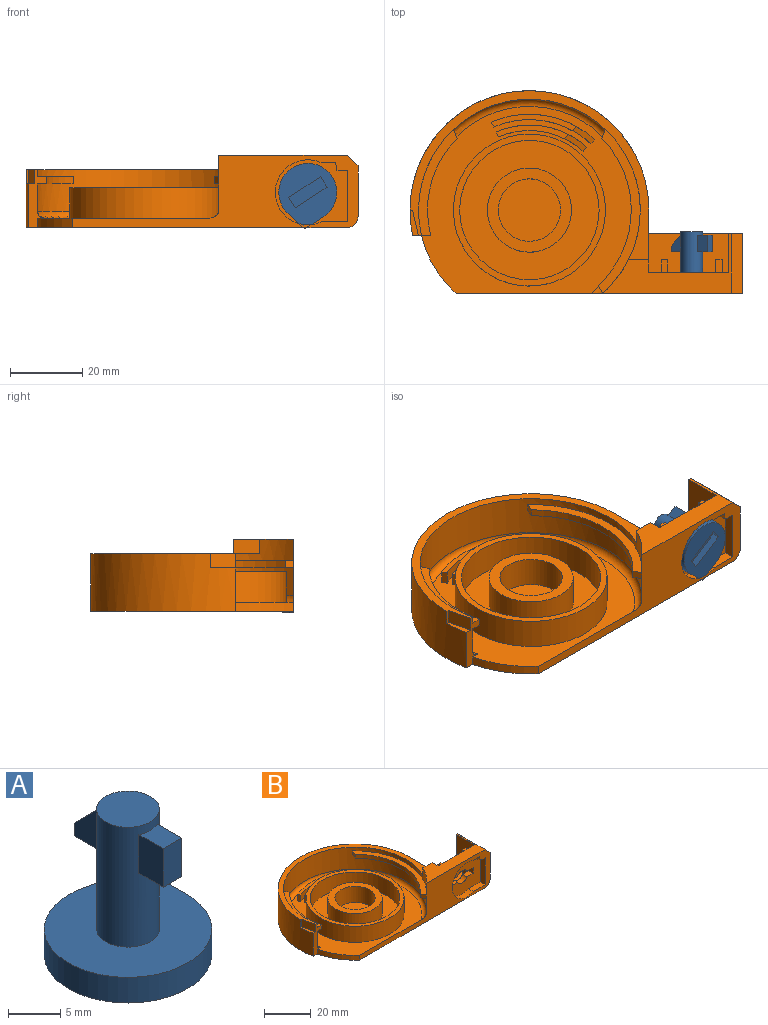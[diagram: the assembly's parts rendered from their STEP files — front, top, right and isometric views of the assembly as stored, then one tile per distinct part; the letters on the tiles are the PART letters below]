
ASSEMBLY  parts=2 mates=1
PART A: 24 faces, bbox 16x16x17 mm
  f0: plane 1.25x0.27mm, normal (0,0,1), area 0.1mm2, adj f11,f19,f23
  f1: plane 6.24x3mm, normal (1,0,0), area 18.7mm2, adj f2,f7,f8,f9
  f2: cylinder r=8mm len=16mm, axis (0,0,1), area 119mm2, adj f1,f7,f8,f9
  f3: plane 10.51x2mm, normal (-1,0,0), area 21mm2, adj f4,f6,f8,f10
  f4: plane 3.4x2mm, normal (0,-1,0), area 6.8mm2, adj f3,f5,f8,f10
  f5: plane 10.51x2mm, normal (1,0,0), area 21mm2, adj f4,f6,f8,f10
  f6: plane 3.4x2mm, normal (0,1,0), area 6.8mm2, adj f3,f5,f8,f10
  f7: plane 6.06x3mm, normal (0.24,0.97,0), area 18.7mm2, adj f1,f2,f8,f9
  f8: plane 16x16mm, normal (0,0,-1), area 172.8mm2, adj f1,f2,f3,f4,f5,f6,f7
  f9: plane 16x16mm, normal (0,0,1), area 180.3mm2, adj f1,f2,f7,f11
  f10: plane 10.51x3.4mm, normal (0,0,-1), area 35.8mm2, adj f3,f4,f5,f6
  f11: cylinder r=3mm len=14mm, axis (0,0,-1), area 240.7mm2, adj f0,f9,f12,f14,f15,f16,f17,f18
  f12: plane 6x6mm, normal (0,0,1), area 28.3mm2, adj f11
  f13: plane 4.5x2.5mm, normal (0,-1,0), area 11.2mm2, adj f14,f15,f16,f17
  f14: plane 4.5x3.27mm, normal (-1,0,0), area 14.7mm2, adj f11,f13,f16,f17
  f15: plane 4.5x3.27mm, normal (1,0,0), area 14.7mm2, adj f11,f13,f16,f17
  f16: plane 3.27x2.5mm, normal (0,0,1), area 7.7mm2, adj f11,f13,f14,f15
  f17: plane 3.27x2.5mm, normal (0,0,-1), area 7.7mm2, adj f11,f13,f14,f15
  f18: plane 4.5x3.27mm, normal (-1,0,0), area 10.2mm2, adj f11,f20,f21,f22,f23
  f19: plane 4.5x3.27mm, normal (1,0,0), area 10.2mm2, adj f0,f11,f20,f21,f23
  f20: plane 2.5x1.5mm, normal (0,1,0), area 3.7mm2, adj f18,f19,f21,f23
  f21: plane 3.27x2.5mm, normal (0,0,-1), area 7.7mm2, adj f11,f18,f19,f20
  f22: plane 1.25x0.27mm, normal (0,0,1), area 0.1mm2, adj f11,f18,f23
  f23: plane 3x3mm, normal (0,0.71,0.71), area 10.6mm2, adj f0,f18,f19,f20,f22
PART B: 75 faces, bbox 92x59.8x20.1 mm
  f0: plane 3.8x2.7mm, normal (0,0,-1), area 10.3mm2, adj f4,f7,f28,f74
  f1: plane 3.8x2.7mm, normal (0,0,-1), area 10.3mm2, adj f5,f7,f28,f74
  f2: plane 3.8x2.7mm, normal (0,0,1), area 10.3mm2, adj f4,f6,f31,f74
  f3: plane 3.8x2.7mm, normal (0,0,1), area 10.3mm2, adj f5,f6,f31,f74
  f4: plane 15.43x6.25mm, normal (1,0,0), area 62.9mm2, adj f0,f2,f11,f28,f31,f36,f37,f74
  f5: plane 15.43x6.25mm, normal (-1,0,0), area 62.9mm2, adj f1,f3,f11,f28,f31,f39,f40,f74
  f6: cylinder r=3.2mm len=5.65mm, axis (0,-1,0), area 18.7mm2, adj f2,f3,f31,f74
  f7: cylinder r=3.2mm len=5.65mm, axis (0,-1,0), area 18.7mm2, adj f0,f1,f28,f74
  f8: cylinder r=30.65mm len=61.3mm, axis (0,0,-1), area 1368.4mm2, adj f9,f10,f19,f25,f26,f56,f57,f59
  f9: plane 16x4.98mm, normal (0,-1,0), area 38.3mm2, adj f8,f10,f20,f21,f24,f27,f41,f43
  f10: plane 66x46.75mm, normal (0,0,1), area 289.6mm2, adj f8,f9,f12,f25,f27,f41,f42
  f11: plane 22x10.8mm, normal (0,0,1), area 225.2mm2, adj f4,f5,f12,f28,f30,f31,f34,f35
  f12: plane 20x17.3mm, normal (1,0,0), area 269.7mm2, adj f10,f11,f24,f25,f26,f27,f28,f34
  f13: plane 38.5x38.5mm, normal (0,0,1), area 739.6mm2, adj f14,f18
  f14: cylinder r=11.62mm len=23.25mm, axis (0,0,-1), area 620.9mm2, adj f13,f17
  f15: plane 17.25x17.25mm, normal (0,0,1), area 233.7mm2, adj f16
  f16: cylinder r=8.62mm len=17.25mm, axis (0,0,-1), area 460.6mm2, adj f15,f17
  f17: plane 23.25x23.25mm, normal (0,0,1), area 190.9mm2, adj f14,f16
  f18: cylinder r=19.25mm len=38.5mm, axis (0,0,-1), area 1028.1mm2, adj f13,f23
  f19: plane 79.01x20.03mm, normal (0,-1,0), area 562mm2, adj f8,f20,f21,f24,f26,f29,f32,f33
  f20: cylinder r=30.65mm len=16mm, axis (0,0,-1), area 47.4mm2, adj f9,f19,f21,f24
  f21: plane 58.49x51.65mm, normal (0,0,1), area 1016.8mm2, adj f9,f19,f20,f22,f45,f46,f47,f48
  f22: cylinder r=21mm len=42mm, axis (0,0,-1), area 1121.5mm2, adj f21,f23
  f23: plane 42x42mm, normal (0,0,1), area 221.3mm2, adj f18,f22
  f24: plane 66x56mm, normal (0,0,-1), area 3117.8mm2, adj f9,f12,f19,f20,f27,f29
  f25: plane 5.61x4mm, normal (0,1,0), area 22.4mm2, adj f8,f10,f12,f26
  f26: plane 35.49x16.5mm, normal (0,0,1), area 218.3mm2, adj f8,f12,f19,f25,f28,f30,f34,f63
  f27: cylinder r=33mm len=66mm, axis (0,0,-1), area 1743.4mm2, adj f9,f10,f12,f24,f42,f43
  f28: plane 22x18.03mm, normal (0,1,0), area 213.7mm2, adj f0,f1,f4,f5,f7,f11,f12,f26
  f29: plane 16.5x0.03mm, normal (-1,0,0), area 0.4mm2, adj f19,f24,f33,f34
  f30: plane 18.03x10.8mm, normal (-1,0,0), area 194.7mm2, adj f11,f26,f28,f34
  f31: plane 13.25x6.21mm, normal (0,1,0), area 75.5mm2, adj f2,f3,f4,f5,f6,f11
  f32: plane 16.5x14.03mm, normal (1,0,0), area 231.4mm2, adj f19,f34,f63,f67
  f33: plane 22.75x16.5mm, normal (0,0,-1), area 375.4mm2, adj f19,f29,f34,f67
  f34: plane 25.75x20.03mm, normal (0,1,0), area 112.7mm2, adj f11,f12,f26,f29,f30,f32,f33,f63
  f35: plane 15.4x3.55mm, normal (-1,0,0), area 54.7mm2, adj f11,f28,f36,f37
  f36: plane 3.55x1.75mm, normal (-0.01,0,1), area 6.2mm2, adj f4,f28,f35,f37
  f37: plane 15.43x1.75mm, normal (0,1,0), area 27mm2, adj f4,f11,f35,f36
  f38: plane 15.43x3.55mm, normal (1,0,0), area 54.8mm2, adj f11,f28,f39,f40
  f39: plane 3.55x1.75mm, normal (0,0,1), area 6.2mm2, adj f5,f28,f38,f40
  f40: plane 15.43x1.75mm, normal (0,1,0), area 27mm2, adj f5,f11,f38,f39
  f41: plane 7x4mm, normal (-0.97,-0.23,0), area 28.7mm2, adj f9,f10,f42,f43
  f42: plane 4x0.7mm, normal (0,-1,0), area 2.8mm2, adj f10,f27,f41,f43
  f43: plane 7x2.33mm, normal (0,0,1), area 8.9mm2, adj f9,f27,f41,f42
  f44: plane 23.62x4.6mm, normal (0,0,1), area 35.4mm2, adj f45,f46,f48,f66
  f45: cylinder r=25mm len=26.85mm, axis (0,0,-1), area 90.3mm2, adj f21,f44,f47,f48,f66
  f46: cylinder r=26.5mm len=28.5mm, axis (0,0,-1), area 96.5mm2, adj f21,f44,f47,f48,f66
  f47: plane 1.1x1.02mm, normal (0.73,-0.68,0), area 0.1mm2, adj f21,f45,f46,f66
  f48: plane 3.5x1.36mm, normal (-0.91,-0.42,0), area 5.3mm2, adj f21,f44,f45,f46
  f49: plane 20.07x3.82mm, normal (0,0,1), area 29.8mm2, adj f50,f51,f53,f65
  f50: cylinder r=22mm len=23.43mm, axis (0,0,-1), area 77.3mm2, adj f21,f49,f52,f53,f65
  f51: cylinder r=23.5mm len=25.03mm, axis (0,0,-1), area 83.4mm2, adj f21,f49,f52,f53,f65
  f52: plane 1.11x1.01mm, normal (0.74,-0.67,0), area 0.1mm2, adj f21,f50,f51,f65
  f53: plane 3.5x1.38mm, normal (-0.92,-0.39,0), area 5.3mm2, adj f21,f49,f50,f51
  f54: cylinder r=28.15mm len=40.59mm, axis (0,0,-1), area 90.7mm2, adj f55,f56,f57,f61
  f55: plane 2.25x2mm, normal (-0.88,-0.48,0), area 5.1mm2, adj f19,f54,f56,f57
  f56: plane 45.35x11.63mm, normal (0,0,1), area 120.5mm2, adj f8,f54,f55,f61
  f57: plane 45.35x11.63mm, normal (0,0,-1), area 120.5mm2, adj f8,f54,f55,f61
  f58: cylinder r=28.15mm len=26.83mm, axis (0,0,-1), area 58.2mm2, adj f9,f59,f60,f62
  f59: plane 29.35x10.67mm, normal (0,0,1), area 76.5mm2, adj f8,f9,f58,f62
  f60: plane 29.35x10.67mm, normal (0,0,-1), area 76.5mm2, adj f8,f9,f58,f62
  f61: plane 2.52x2mm, normal (-0.93,0.37,0), area 5.4mm2, adj f8,f54,f56,f57
  f62: plane 2.52x2mm, normal (0.93,0.37,0), area 5.4mm2, adj f8,f58,f59,f60
  f63: plane 16.5x3mm, normal (0.71,0,0.71), area 70mm2, adj f19,f26,f32,f34
  f64: torus R=28.65mm, axis (0,0,1), area 400mm2, adj f8,f9,f19,f21
  f65: plane 6.04x4.61mm, normal (0.37,-0.34,0.87), area 10.5mm2, adj f49,f50,f51,f52
  f66: plane 5.95x4.69mm, normal (0.37,-0.34,0.87), area 10.5mm2, adj f44,f45,f46,f47
  f67: cylinder r=3mm len=16.5mm, axis (0,-1,0), area 77.8mm2, adj f19,f32,f33,f34
  f68: cylinder r=9mm len=18mm, axis (0,-1,0), area 107.9mm2, adj f19,f69,f73,f74
  f69: plane 7.25x3mm, normal (0,0,1), area 21.8mm2, adj f19,f68,f70,f74
  f70: plane 14.16x3mm, normal (-1,0,0), area 42.5mm2, adj f19,f69,f71,f74
  f71: plane 3x2.95mm, normal (0,0,-1), area 8.8mm2, adj f19,f70,f72,f74
  f72: plane 3x2.22mm, normal (-0.98,0,-0.18), area 6.8mm2, adj f19,f71,f73,f74
  f73: plane 3.95x3mm, normal (0,0,-1), area 11.9mm2, adj f19,f68,f72,f74
  f74: plane 20.01x18mm, normal (0,-1,0), area 251.2mm2, adj f0,f1,f2,f3,f4,f5,f6,f7
PLACE A rot(axis=(-0.79,0.43,0.43),103.1deg) t=(28.45,-13.13,13.28)mm
PLACE B t=(-14.56,6.87,0.74)mm fixed
MATE revolute A.f2 <-> B.f68  axis (0,1,0) through (30.32,-13.13,10.43)mm
